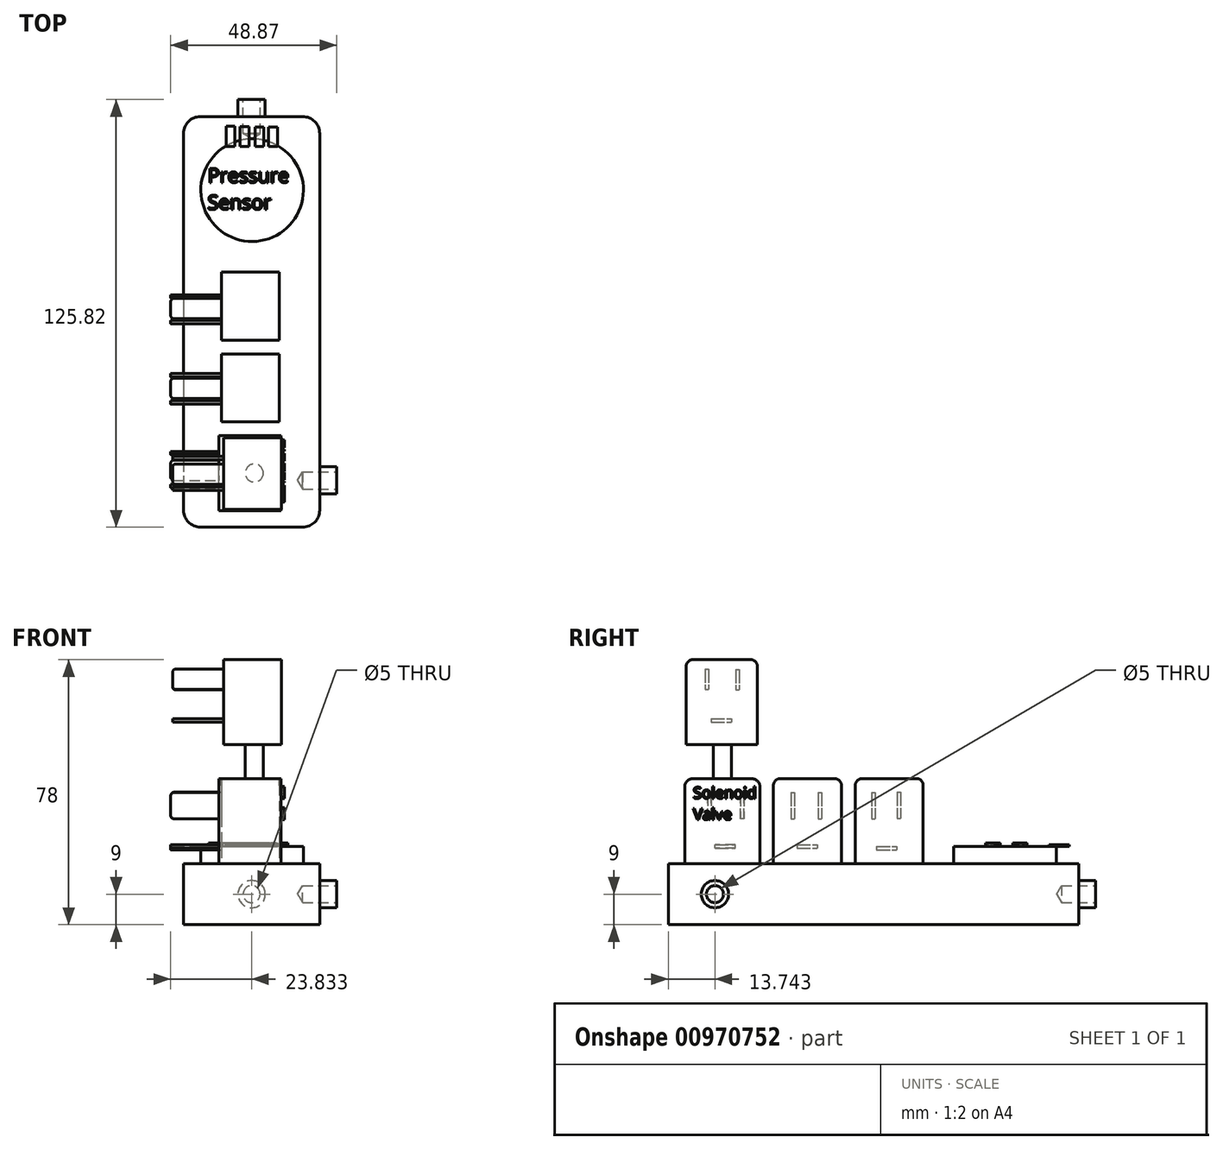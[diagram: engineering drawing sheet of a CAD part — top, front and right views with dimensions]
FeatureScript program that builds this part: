
annotation { "Feature Type Name" : "Feature", "Feature Type Description" : "" }
export const myFeature = defineFeature(function(context is Context, id is Id, definition is map)
    precondition{}
    {
        {
            var Q0;
            Q0=qCreatedBy(makeId("Top.planeOp"),FACE);
            var sketch = newSketch(context, id + "F0", { "sketchPlane" : qUnion([Q0])});
            skLineSegment(sketch, "E0", {"start": v(-31.16, -51.49) * mm, "end": v(8.92, -51.49) * mm});
            skLineSegment(sketch, "E1", {"start": v(8.92, -51.49) * mm, "end": v(8.92, 69.33) * mm});
            skLineSegment(sketch, "E2", {"start": v(8.92, 69.33) * mm, "end": v(-31.16, 69.33) * mm});
            skLineSegment(sketch, "E3", {"start": v(-31.16, 69.33) * mm, "end": v(-31.16, -51.49) * mm});
            skSolve(sketch);
        }
        {
            var Q0;
            Q0=makeQuery(id+"F0.imprint","IMPRINT",FACE,{"disambiguationData":[TD([[makeQuery(id+"F0.imprint","IMPRINT",EDGE,{"derivedFrom":sQuery(id+"F0.wireOp",EDGE,"E0")}),1.0]])]});
            extrude(context, id + "F1", {"entities" : qUnion([Q0]), "depth" : 18 * mm, "offsetDistance" : 25 * mm});
        }
        {
            var Q0;
            Q0=makeQuery(id+"F1.opExtrude","CAP_FACE",FACE,{"disambiguationData":[OSD([sQuery(id+"F0.wireOp",EDGE,"E0"),sQuery(id+"F0.wireOp",EDGE,"E1"),sQuery(id+"F0.wireOp",EDGE,"E2"),sQuery(id+"F0.wireOp",EDGE,"E3")])],"isStart":false});
            var sketch = newSketch(context, id + "F2", { "sketchPlane" : qUnion([Q0])});
            skCircle(sketch, "E4", {"center": v(-10.96, 47.67) * mm, "radius": 15.1 * mm});
            skSolve(sketch);
        }
        {
            var Q0;
            Q0=makeQuery(id+"F2.imprint","IMPRINT",FACE,{"disambiguationData":[TD([[makeQuery(id+"F2.imprint","IMPRINT",EDGE,{"derivedFrom":sQuery(id+"F2.wireOp",EDGE,"E4")}),1.0]])]});
            extrude(context, id + "F3", {"entities" : qUnion([Q0]), "operationType" : NewBodyOperationType.ADD, "depth" : 5 * mm, "offsetDistance" : 25 * mm});
        }
        {
            var Q0;
            Q0=makeQuery(id+"F3.opExtrude","CAP_FACE",FACE,{"disambiguationData":[OSD([sQuery(id+"F2.wireOp",EDGE,"E4")])],"isStart":false});
            var sketch = newSketch(context, id + "F4", { "sketchPlane" : qUnion([Q0])});
            skLineSegment(sketch, "E5", {"start": v(-14.48, 60.58) * mm, "end": v(-11.85, 60.58) * mm});
            skLineSegment(sketch, "E6", {"start": v(-11.85, 60.58) * mm, "end": v(-11.85, 66.33) * mm});
            skLineSegment(sketch, "E7", {"start": v(-11.85, 66.33) * mm, "end": v(-14.55, 66.33) * mm});
            skLineSegment(sketch, "E8", {"start": v(-14.55, 66.33) * mm, "end": v(-14.48, 60.58) * mm});
            skSolve(sketch);
        }
        {
            var Q0;
            {var subQ0=sQuery(id+"F4.wireOp",EDGE,"E7");Q0=makeQuery(id+"F4.imprint","IMPRINT",FACE,{"disambiguationData":[TD([[makeQuery(id+"F4.imprint","IMPRINT",EDGE,{"derivedFrom":subQ0}),1.0]])]});}
            var Q1;
            {var subQ0=sQuery(id+"F4.wireOp",EDGE,"E5");Q1=makeQuery(id+"F4.imprint","IMPRINT",FACE,{"disambiguationData":[TD([[makeQuery(id+"F4.imprint","IMPRINT",EDGE,{"derivedFrom":subQ0}),1.0]])]});}
            extrude(context, id + "F5", {"entities" : qUnion([Q0, Q1]), "operationType" : NewBodyOperationType.ADD, "depth" : 0.5 * mm, "offsetDistance" : 25 * mm});
        }
        {
            var Q0;
            Q0=makeQuery(id+"F3.opExtrude","CAP_FACE",FACE,{"disambiguationData":[OSD([sQuery(id+"F2.wireOp",EDGE,"E4")])],"isStart":false});
            var sketch = newSketch(context, id + "F6", { "sketchPlane" : qUnion([Q0])});
            skLineSegment(sketch, "E9", {"start": v(-16.09, 60.58) * mm, "end": v(-18.63, 60.58) * mm});
            skLineSegment(sketch, "E10", {"start": v(-18.63, 60.58) * mm, "end": v(-18.63, 66.5) * mm});
            skLineSegment(sketch, "E11", {"start": v(-18.63, 66.5) * mm, "end": v(-16.09, 66.5) * mm});
            skLineSegment(sketch, "E12", {"start": v(-16.09, 66.5) * mm, "end": v(-16.09, 60.58) * mm});
            skSolve(sketch);
        }
        {
            var Q0;
            {var subQ0=sQuery(id+"F6.wireOp",EDGE,"E9");Q0=makeQuery(id+"F6.imprint","IMPRINT",FACE,{"disambiguationData":[TD([[makeQuery(id+"F6.imprint","IMPRINT",EDGE,{"derivedFrom":subQ0}),-1.0]])]});}
            var Q1;
            {var subQ0=sQuery(id+"F6.wireOp",EDGE,"E11");Q1=makeQuery(id+"F6.imprint","IMPRINT",FACE,{"disambiguationData":[TD([[makeQuery(id+"F6.imprint","IMPRINT",EDGE,{"derivedFrom":subQ0}),-1.0]])]});}
            extrude(context, id + "F7", {"entities" : qUnion([Q0, Q1]), "operationType" : NewBodyOperationType.ADD, "depth" : 0.5 * mm, "offsetDistance" : 25 * mm});
        }
        {
            var Q0;
            Q0=makeQuery(id+"F3.opExtrude","CAP_FACE",FACE,{"disambiguationData":[OSD([sQuery(id+"F2.wireOp",EDGE,"E4")])],"isStart":false});
            var sketch = newSketch(context, id + "F8", { "sketchPlane" : qUnion([Q0])});
            skLineSegment(sketch, "E13", {"start": v(-10.12, 60.58) * mm, "end": v(-7.57, 60.58) * mm});
            skLineSegment(sketch, "E14", {"start": v(-7.57, 60.58) * mm, "end": v(-7.57, 66.29) * mm});
            skLineSegment(sketch, "E15", {"start": v(-7.57, 66.29) * mm, "end": v(-10.12, 66.29) * mm});
            skLineSegment(sketch, "E16", {"start": v(-10.12, 66.29) * mm, "end": v(-10.12, 60.58) * mm});
            skSolve(sketch);
        }
        {
            var Q0;
            {var subQ0=sQuery(id+"F8.wireOp",EDGE,"E15");Q0=makeQuery(id+"F8.imprint","IMPRINT",FACE,{"disambiguationData":[TD([[makeQuery(id+"F8.imprint","IMPRINT",EDGE,{"derivedFrom":subQ0}),1.0]])]});}
            var Q1;
            {var subQ0=sQuery(id+"F8.wireOp",EDGE,"E13");Q1=makeQuery(id+"F8.imprint","IMPRINT",FACE,{"disambiguationData":[TD([[makeQuery(id+"F8.imprint","IMPRINT",EDGE,{"derivedFrom":subQ0}),1.0]])]});}
            extrude(context, id + "F9", {"entities" : qUnion([Q0, Q1]), "operationType" : NewBodyOperationType.ADD, "depth" : 0.5 * mm, "offsetDistance" : 25 * mm});
        }
        {
            var Q0;
            Q0=makeQuery(id+"F3.opExtrude","CAP_FACE",FACE,{"disambiguationData":[OSD([sQuery(id+"F2.wireOp",EDGE,"E4")])],"isStart":false});
            var sketch = newSketch(context, id + "F10", { "sketchPlane" : qUnion([Q0])});
            skText(sketch, "E17", { "text": "Pressure\nSensor", "fontName": "OpenSans-Regular.ttf"});
            const initialGuessF10  = {"E17": [-0.02405, 0.04993, 1, 0, 0.0042]};
            skSetInitialGuess(sketch, initialGuessF10);
            skSolve(sketch);
        }
        {
            var Q0;
            Q0=qSketchRegion(id+"F10",true);
            extrude(context, id + "F11", {"entities" : qUnion([Q0]), "operationType" : NewBodyOperationType.ADD, "depth" : 1 * mm, "offsetDistance" : 25 * mm});
        }
        {
            var Q0;
            Q0=makeQuery(id+"F1.opExtrude","SWEPT_FACE",FACE,{"disambiguationData":[OSD([sQuery(id+"F0.wireOp",EDGE,"E2")])]});
            var sketch = newSketch(context, id + "F12", { "sketchPlane" : qUnion([Q0])});
            skCircle(sketch, "E18", {"center": v(11.12, 9) * mm, "radius": 4 * mm});
            skPoint(sketch, "E18.centerSnap0", {"position": v(31.16, 9) * mm});
            skPoint(sketch, "E18.centerSnap1", {"position": v(11.12, 18) * mm});
            skSolve(sketch);
        }
        {
            var Q0;
            Q0=makeQuery(id+"F12.imprint","IMPRINT",FACE,{"disambiguationData":[TD([[makeQuery(id+"F12.imprint","IMPRINT",EDGE,{"derivedFrom":sQuery(id+"F12.wireOp",EDGE,"E18")}),1.0]])]});
            extrude(context, id + "F13", {"entities" : qUnion([Q0]), "operationType" : NewBodyOperationType.ADD, "depth" : 5 * mm, "offsetDistance" : 25 * mm});
        }
        {
            var Q0;
            Q0=makeQuery(id+"F13.opExtrude","CAP_FACE",FACE,{"disambiguationData":[OSD([sQuery(id+"F12.wireOp",EDGE,"E18")])],"isStart":false});
            var sketch = newSketch(context, id + "F14", { "sketchPlane" : qUnion([Q0])});
            skCircle(sketch, "E19", {"center": v(11.12, 9) * mm, "radius": 2.5 * mm});
            skSolve(sketch);
        }
        {
            var Q0;
            Q0=sQuery(id+"F14.wireOp",VERTEX,"E19.center");
            var Q1;
            Q1=makeQuery(id+"F1.opExtrude","SWEPT_BODY",BODY,{"disambiguationData":[OSD([sQuery(id+"F0.wireOp",EDGE,"E0"),sQuery(id+"F0.wireOp",EDGE,"E1"),sQuery(id+"F0.wireOp",EDGE,"E2"),sQuery(id+"F0.wireOp",EDGE,"E3")])]});
            hole(context, id + "F15", {"style" : HoleStyle.SIMPLE, "endStyle" : HoleEndStyle.BLIND, "holeDiameter" : 5 * mm, "majorDiameter" : 5 * mm, "holeDepth" : 10 * mm, "isTappedThrough" : true, "tappedDepth" : 12 * mm, "tapClearance" : 3, "locations" : qUnion([Q0]), "scope" : qUnion([Q1])});
        }
        {
            var Q0;
            {var subQ7=sQuery(id+"F2.wireOp",EDGE,"E4");Q0=makeQuery(id+"F11.boolean.opBoolean","SPLIT",FACE,{"disambiguationData":[TD([makeQuery(id+"F3.opExtrude","SWEPT_FACE",FACE,{"disambiguationData":[OSD([subQ7])]})])],"derivedFrom":makeQuery(id+"F3.opExtrude","CAP_FACE",FACE,{"disambiguationData":[OSD([subQ7])],"isStart":false})});}
            var sketch = newSketch(context, id + "F16", { "sketchPlane" : qUnion([Q0])});
            skLineSegment(sketch, "E20.bottom", {"start": v(-6.1, 60.58) * mm, "end": v(-3.42, 60.58) * mm});
            skLineSegment(sketch, "E20.top", {"start": v(-6.1, 66.26) * mm, "end": v(-3.42, 66.26) * mm});
            skLineSegment(sketch, "E20.left", {"start": v(-6.1, 60.58) * mm, "end": v(-6.1, 66.26) * mm});
            skLineSegment(sketch, "E20.right", {"start": v(-3.42, 60.58) * mm, "end": v(-3.42, 66.26) * mm});
            skSolve(sketch);
        }
        {
            var Q0;
            {var subQ0=sQuery(id+"F16.wireOp",EDGE,"E20.bottom");Q0=makeQuery(id+"F16.imprint","IMPRINT",FACE,{"disambiguationData":[TD([[makeQuery(id+"F16.imprint","IMPRINT",EDGE,{"derivedFrom":subQ0}),1.0]])]});}
            var Q1;
            {var subQ0=sQuery(id+"F16.wireOp",EDGE,"E20.top");Q1=makeQuery(id+"F16.imprint","IMPRINT",FACE,{"disambiguationData":[TD([[makeQuery(id+"F16.imprint","IMPRINT",EDGE,{"derivedFrom":subQ0}),-1.0]])]});}
            extrude(context, id + "F17", {"entities" : qUnion([Q0, Q1]), "operationType" : NewBodyOperationType.ADD, "depth" : 0.5 * mm, "offsetDistance" : 25 * mm});
        }
        {
            var Q0;
            Q0=makeQuery(id+"F1.opExtrude","SWEPT_FACE",FACE,{"disambiguationData":[OSD([sQuery(id+"F0.wireOp",EDGE,"E1")])]});
            var sketch = newSketch(context, id + "F18", { "sketchPlane" : qUnion([Q0])});
            skCircle(sketch, "E21", {"center": v(-37.75, 9) * mm, "radius": 4 * mm});
            skPoint(sketch, "E21.centerSnap0", {"position": v(-51.49, 9) * mm});
            skSolve(sketch);
        }
        {
            var Q0;
            Q0=makeQuery(id+"F18.imprint","IMPRINT",FACE,{"disambiguationData":[TD([[makeQuery(id+"F18.imprint","IMPRINT",EDGE,{"derivedFrom":sQuery(id+"F18.wireOp",EDGE,"E21")}),1.0]])]});
            extrude(context, id + "F19", {"entities" : qUnion([Q0]), "operationType" : NewBodyOperationType.ADD, "depth" : 5 * mm, "offsetDistance" : 25 * mm});
        }
        {
            var Q0;
            Q0=makeQuery(id+"F19.opExtrude","CAP_FACE",FACE,{"disambiguationData":[OSD([sQuery(id+"F18.wireOp",EDGE,"E21")])],"isStart":false});
            var sketch = newSketch(context, id + "F20", { "sketchPlane" : qUnion([Q0])});
            skCircle(sketch, "E22", {"center": v(-37.75, 9) * mm, "radius": 2.01 * mm});
            skSolve(sketch);
        }
        {
            var Q0;
            Q0=sQuery(id+"F20.wireOp",VERTEX,"E22.center");
            var Q1;
            Q1=makeQuery(id+"F1.opExtrude","SWEPT_BODY",BODY,{"disambiguationData":[OSD([sQuery(id+"F0.wireOp",EDGE,"E0"),sQuery(id+"F0.wireOp",EDGE,"E1"),sQuery(id+"F0.wireOp",EDGE,"E2"),sQuery(id+"F0.wireOp",EDGE,"E3")])]});
            hole(context, id + "F21", {"style" : HoleStyle.SIMPLE, "endStyle" : HoleEndStyle.BLIND, "holeDiameter" : 5 * mm, "majorDiameter" : 5 * mm, "holeDepth" : 10 * mm, "isTappedThrough" : true, "tappedDepth" : 12 * mm, "tapClearance" : 3, "locations" : qUnion([Q0]), "scope" : qUnion([Q1])});
        }
        {
            var Q0;
            Q0=makeQuery(id+"F1.opExtrude","SWEPT_EDGE",EDGE,{"disambiguationData":[OSD([sQuery(id+"F0.wireOp",EDGE,"E1"),sQuery(id+"F0.wireOp",EDGE,"E2")])]});
            fillet(context, id + "F22", {"entities" : qUnion([Q0]), "radius" : 5 * mm, "tangentPropagation" : true, "allowEdgeOverflow" : false});
        }
        {
            var Q0;
            Q0=makeQuery(id+"F1.opExtrude","SWEPT_EDGE",EDGE,{"disambiguationData":[OSD([sQuery(id+"F0.wireOp",EDGE,"E2"),sQuery(id+"F0.wireOp",EDGE,"E3")])]});
            fillet(context, id + "F23", {"entities" : qUnion([Q0]), "radius" : 5 * mm, "tangentPropagation" : true, "allowEdgeOverflow" : false});
        }
        {
            var Q0;
            Q0=makeQuery(id+"F1.opExtrude","SWEPT_EDGE",EDGE,{"disambiguationData":[OSD([sQuery(id+"F0.wireOp",EDGE,"E0"),sQuery(id+"F0.wireOp",EDGE,"E3")])]});
            fillet(context, id + "F24", {"entities" : qUnion([Q0]), "radius" : 5 * mm, "tangentPropagation" : true, "allowEdgeOverflow" : false});
        }
        {
            var Q0;
            Q0=makeQuery(id+"F1.opExtrude","SWEPT_EDGE",EDGE,{"disambiguationData":[OSD([sQuery(id+"F0.wireOp",EDGE,"E0"),sQuery(id+"F0.wireOp",EDGE,"E1")])]});
            fillet(context, id + "F25", {"entities" : qUnion([Q0]), "radius" : 5 * mm, "tangentPropagation" : true, "allowEdgeOverflow" : false});
        }
        {
            var Q0;
            Q0=makeQuery(id+"F1.opExtrude","CAP_FACE",FACE,{"disambiguationData":[OSD([sQuery(id+"F0.wireOp",EDGE,"E0"),sQuery(id+"F0.wireOp",EDGE,"E1"),sQuery(id+"F0.wireOp",EDGE,"E2"),sQuery(id+"F0.wireOp",EDGE,"E3")])],"isStart":false});
            var sketch = newSketch(context, id + "F26", { "sketchPlane" : qUnion([Q0])});
            skLineSegment(sketch, "E23.bottom", {"start": v(-20.72, -46.66) * mm, "end": v(-2.41, -46.66) * mm});
            skLineSegment(sketch, "E23.top", {"start": v(-20.72, -24.5) * mm, "end": v(-2.41, -24.5) * mm});
            skLineSegment(sketch, "E23.left", {"start": v(-20.72, -46.66) * mm, "end": v(-20.72, -24.5) * mm});
            skLineSegment(sketch, "E23.right", {"start": v(-2.41, -46.66) * mm, "end": v(-2.41, -24.5) * mm});
            skSolve(sketch);
        }
        {
            var Q0;
            Q0=makeQuery(id+"F26.imprint","IMPRINT",FACE,{"disambiguationData":[TD([[makeQuery(id+"F26.imprint","IMPRINT",EDGE,{"derivedFrom":sQuery(id+"F26.wireOp",EDGE,"E23.bottom")}),1.0]])]});
            extrude(context, id + "F27", {"entities" : qUnion([Q0]), "operationType" : NewBodyOperationType.ADD, "depth" : 25 * mm, "offsetDistance" : 25 * mm});
        }
        {
            var Q0;
            Q0=makeQuery(id+"F27.opExtrude","CAP_EDGE",EDGE,{"disambiguationData":[OSD([sQuery(id+"F26.wireOp",EDGE,"E23.bottom")])],"isStart":false});
            var Q1;
            Q1=makeQuery(id+"F27.opExtrude","CAP_EDGE",EDGE,{"disambiguationData":[OSD([sQuery(id+"F26.wireOp",EDGE,"E23.top")])],"isStart":false});
            fillet(context, id + "F28", {"entities" : qUnion([Q0, Q1]), "radius" : 2.5 * mm, "tangentPropagation" : true, "allowEdgeOverflow" : false});
        }
        {
            var Q0;
            Q0=makeQuery(id+"F27.opExtrude","SWEPT_FACE",FACE,{"disambiguationData":[OSD([sQuery(id+"F26.wireOp",EDGE,"E23.right")])]});
            var sketch = newSketch(context, id + "F29", { "sketchPlane" : qUnion([Q0])});
            skText(sketch, "E24", { "text": "Solenoid\nValve", "fontName": "OpenSans-Regular.ttf"});
            const initialGuessF29  = {"E24": [-0.04416, 0.03718, 1, 0, 0.00332]};
            skSetInitialGuess(sketch, initialGuessF29);
            skSolve(sketch);
        }
        {
            var Q0;
            Q0=qSketchRegion(id+"F29",true);
            extrude(context, id + "F30", {"entities" : qUnion([Q0]), "operationType" : NewBodyOperationType.ADD, "depth" : 1 * mm, "offsetDistance" : 25 * mm});
        }
        {
            var Q0;
            Q0=makeQuery(id+"F1.opExtrude","CAP_FACE",FACE,{"disambiguationData":[OSD([sQuery(id+"F0.wireOp",EDGE,"E0"),sQuery(id+"F0.wireOp",EDGE,"E1"),sQuery(id+"F0.wireOp",EDGE,"E2"),sQuery(id+"F0.wireOp",EDGE,"E3")])],"isStart":false});
            var sketch = newSketch(context, id + "F31", { "sketchPlane" : qUnion([Q0])});
            skLineSegment(sketch, "E25.bottom", {"start": v(-3, -0.51) * mm, "end": v(-20, -0.51) * mm});
            skLineSegment(sketch, "E25.top", {"start": v(-3, -20.51) * mm, "end": v(-20, -20.51) * mm});
            skLineSegment(sketch, "E25.left", {"start": v(-3, -0.51) * mm, "end": v(-3, -20.51) * mm});
            skLineSegment(sketch, "E25.right", {"start": v(-20, -0.51) * mm, "end": v(-20, -20.51) * mm});
            skLineSegment(sketch, "E26.bottom", {"start": v(-2.95, 23.55) * mm, "end": v(-19.95, 23.55) * mm});
            skLineSegment(sketch, "E26.top", {"start": v(-2.95, 3.55) * mm, "end": v(-19.95, 3.55) * mm});
            skLineSegment(sketch, "E26.left", {"start": v(-2.95, 23.55) * mm, "end": v(-2.95, 3.55) * mm});
            skLineSegment(sketch, "E26.right", {"start": v(-19.95, 23.55) * mm, "end": v(-19.95, 3.55) * mm});
            skSolve(sketch);
        }
        {
            var Q0;
            Q0 = qSketchRegion(id + "F31", true);
            extrude(context, id + "F32", {"entities" : qUnion([Q0]), "operationType" : NewBodyOperationType.ADD, "depth" : 25 * mm, "offsetDistance" : 25 * mm});
        }
        {
            var Q0;
            Q0=makeQuery(id+"F32.opExtrude","CAP_EDGE",EDGE,{"disambiguationData":[OSD([sQuery(id+"F31.wireOp",EDGE,"E25.bottom")])],"isStart":false});
            var Q1;
            Q1=makeQuery(id+"F32.opExtrude","CAP_EDGE",EDGE,{"disambiguationData":[OSD([sQuery(id+"F31.wireOp",EDGE,"E25.top")])],"isStart":false});
            var Q2;
            Q2=makeQuery(id+"F32.opExtrude","CAP_EDGE",EDGE,{"disambiguationData":[OSD([sQuery(id+"F31.wireOp",EDGE,"E26.top")])],"isStart":false});
            var Q3;
            Q3=makeQuery(id+"F32.opExtrude","CAP_EDGE",EDGE,{"disambiguationData":[OSD([sQuery(id+"F31.wireOp",EDGE,"E26.bottom")])],"isStart":false});
            fillet(context, id + "F33", {"entities" : qUnion([Q0, Q1, Q2, Q3]), "radius" : 2 * mm, "tangentPropagation" : true, "allowEdgeOverflow" : false});
        }
        {
            var Q0;
            Q0=makeQuery(id+"F32.opExtrude","SWEPT_FACE",FACE,{"disambiguationData":[OSD([sQuery(id+"F31.wireOp",EDGE,"E26.right")])]});
            cPlane(context, id + "F34", {"entities" : qUnion([Q0]), "cplaneType" : CPlaneType.OFFSET, "offset" : 0 * mm, "width" : 150 * mm, "height" : 150 * mm});
        }
        {
            var Q0;
            Q0=qCreatedBy(id+"F34.planeOp",FACE);
            var sketch = newSketch(context, id + "F35", { "sketchPlane" : qUnion([Q0])});
            skLineSegment(sketch, "E27.bottom", {"start": v(-8.35, 38.88) * mm, "end": v(-9.35, 38.88) * mm});
            skLineSegment(sketch, "E27.top", {"start": v(-8.35, 31.16) * mm, "end": v(-9.35, 31.16) * mm});
            skLineSegment(sketch, "E27.left", {"start": v(-8.35, 38.88) * mm, "end": v(-8.35, 31.16) * mm});
            skLineSegment(sketch, "E27.right", {"start": v(-9.35, 38.88) * mm, "end": v(-9.35, 31.16) * mm});
            skLineSegment(sketch, "E28.bottom", {"start": v(-15.9, 38.98) * mm, "end": v(-16.9, 38.98) * mm});
            skLineSegment(sketch, "E28.top", {"start": v(-15.9, 31.26) * mm, "end": v(-16.9, 31.26) * mm});
            skLineSegment(sketch, "E28.left", {"start": v(-15.9, 38.98) * mm, "end": v(-15.9, 31.26) * mm});
            skLineSegment(sketch, "E28.right", {"start": v(-16.9, 38.98) * mm, "end": v(-16.9, 31.26) * mm});
            skLineSegment(sketch, "E29.bottom", {"start": v(15.3, 38.88) * mm, "end": v(14.3, 38.88) * mm});
            skLineSegment(sketch, "E29.top", {"start": v(15.3, 31.16) * mm, "end": v(14.3, 31.16) * mm});
            skLineSegment(sketch, "E29.left", {"start": v(15.3, 38.88) * mm, "end": v(15.3, 31.16) * mm});
            skLineSegment(sketch, "E29.right", {"start": v(14.3, 38.88) * mm, "end": v(14.3, 31.16) * mm});
            skLineSegment(sketch, "E30.bottom", {"start": v(7.3, 38.88) * mm, "end": v(6.3, 38.88) * mm});
            skLineSegment(sketch, "E30.top", {"start": v(7.3, 31.16) * mm, "end": v(6.3, 31.16) * mm});
            skLineSegment(sketch, "E30.left", {"start": v(7.3, 38.88) * mm, "end": v(7.3, 31.16) * mm});
            skLineSegment(sketch, "E30.right", {"start": v(6.3, 38.88) * mm, "end": v(6.3, 31.16) * mm});
            skLineSegment(sketch, "E31.bottom", {"start": v(30.2, 38.87) * mm, "end": v(29.2, 38.87) * mm});
            skLineSegment(sketch, "E31.top", {"start": v(30.2, 31.15) * mm, "end": v(29.2, 31.15) * mm});
            skLineSegment(sketch, "E31.left", {"start": v(30.2, 38.87) * mm, "end": v(30.2, 31.15) * mm});
            skLineSegment(sketch, "E31.right", {"start": v(29.2, 38.87) * mm, "end": v(29.2, 31.15) * mm});
            skLineSegment(sketch, "E32.bottom", {"start": v(39.9, 38.91) * mm, "end": v(38.9, 38.91) * mm});
            skLineSegment(sketch, "E32.top", {"start": v(39.9, 31.19) * mm, "end": v(38.9, 31.19) * mm});
            skLineSegment(sketch, "E32.left", {"start": v(39.9, 38.91) * mm, "end": v(39.9, 31.19) * mm});
            skLineSegment(sketch, "E32.right", {"start": v(38.9, 38.91) * mm, "end": v(38.9, 31.19) * mm});
            skLineSegment(sketch, "E33.bottom", {"start": v(37.73, 23.51) * mm, "end": v(31.73, 23.51) * mm});
            skLineSegment(sketch, "E33.top", {"start": v(37.73, 22.51) * mm, "end": v(31.73, 22.51) * mm});
            skLineSegment(sketch, "E33.left", {"start": v(37.73, 23.51) * mm, "end": v(37.73, 22.51) * mm});
            skLineSegment(sketch, "E33.right", {"start": v(31.73, 23.51) * mm, "end": v(31.73, 22.51) * mm});
            skLineSegment(sketch, "E34.bottom", {"start": v(13.65, 23.52) * mm, "end": v(7.65, 23.52) * mm});
            skLineSegment(sketch, "E34.top", {"start": v(13.65, 22.52) * mm, "end": v(7.65, 22.52) * mm});
            skLineSegment(sketch, "E34.left", {"start": v(13.65, 23.52) * mm, "end": v(13.65, 22.52) * mm});
            skLineSegment(sketch, "E34.right", {"start": v(7.65, 23.52) * mm, "end": v(7.65, 22.52) * mm});
            skLineSegment(sketch, "E35.bottom", {"start": v(-9.82, 23.03) * mm, "end": v(-15.82, 23.03) * mm});
            skLineSegment(sketch, "E35.top", {"start": v(-9.82, 22.03) * mm, "end": v(-15.82, 22.03) * mm});
            skLineSegment(sketch, "E35.left", {"start": v(-9.82, 23.03) * mm, "end": v(-9.82, 22.03) * mm});
            skLineSegment(sketch, "E35.right", {"start": v(-15.82, 23.03) * mm, "end": v(-15.82, 22.03) * mm});
            skSolve(sketch);
        }
        {
            var Q0;
            Q0 = qSketchRegion(id + "F35", true);
            extrude(context, id + "F36", {"entities" : qUnion([Q0]), "operationType" : NewBodyOperationType.ADD, "depth" : 15 * mm, "offsetDistance" : 25 * mm});
        }
        {
            var Q0;
            Q0=makeQuery(id+"F27.opExtrude","CAP_FACE",FACE,{"disambiguationData":[OSD([sQuery(id+"F26.wireOp",EDGE,"E23.bottom"),sQuery(id+"F26.wireOp",EDGE,"E23.top"),sQuery(id+"F26.wireOp",EDGE,"E23.left"),sQuery(id+"F26.wireOp",EDGE,"E23.right")])],"isStart":false});
            var sketch = newSketch(context, id + "F37", { "sketchPlane" : qUnion([Q0])});
            skCircle(sketch, "E36", {"center": v(-10.33, -35.58) * mm, "radius": 2.67 * mm});
            skPoint(sketch, "E36.centerSnap0", {"position": v(-2.41, -35.58) * mm});
            skSolve(sketch);
        }
        {
            var Q0;
            Q0 = qSketchRegion(id + "F37", true);
            extrude(context, id + "F38", {"entities" : qUnion([Q0]), "operationType" : NewBodyOperationType.ADD, "depth" : 10 * mm, "offsetDistance" : 25 * mm});
        }
        {
            var Q0;
            Q0=makeQuery(id+"F38.opExtrude","CAP_FACE",FACE,{"disambiguationData":[OSD([sQuery(id+"F37.wireOp",EDGE,"E36")])],"isStart":false});
            var sketch = newSketch(context, id + "F39", { "sketchPlane" : qUnion([Q0])});
            skLineSegment(sketch, "E37.bottom", {"start": v(-2.4, -46.23) * mm, "end": v(-19.4, -46.23) * mm});
            skLineSegment(sketch, "E37.top", {"start": v(-2.4, -25.23) * mm, "end": v(-19.4, -25.23) * mm});
            skLineSegment(sketch, "E37.left", {"start": v(-2.4, -46.23) * mm, "end": v(-2.4, -25.23) * mm});
            skLineSegment(sketch, "E37.right", {"start": v(-19.4, -46.23) * mm, "end": v(-19.4, -25.23) * mm});
            skSolve(sketch);
        }
        {
            var Q0;
            Q0 = qSketchRegion(id + "F39", true);
            extrude(context, id + "F40", {"entities" : qUnion([Q0]), "operationType" : NewBodyOperationType.ADD, "depth" : 25 * mm, "offsetDistance" : 25 * mm});
        }
        {
            var Q0;
            Q0=makeQuery(id+"F40.opExtrude","CAP_EDGE",EDGE,{"disambiguationData":[OSD([sQuery(id+"F39.wireOp",EDGE,"E37.top")])],"isStart":false});
            var Q1;
            Q1=makeQuery(id+"F40.opExtrude","CAP_EDGE",EDGE,{"disambiguationData":[OSD([sQuery(id+"F39.wireOp",EDGE,"E37.bottom")])],"isStart":false});
            fillet(context, id + "F41", {"entities" : qUnion([Q0, Q1]), "radius" : 2 * mm, "tangentPropagation" : true, "allowEdgeOverflow" : false});
        }
        {
            var Q0;
            Q0=makeQuery(id+"F40.opExtrude","SWEPT_FACE",FACE,{"disambiguationData":[OSD([sQuery(id+"F39.wireOp",EDGE,"E37.right")])]});
            var sketch = newSketch(context, id + "F42", { "sketchPlane" : qUnion([Q0])});
            skLineSegment(sketch, "E38.bottom", {"start": v(40.66, 75.23) * mm, "end": v(39.66, 75.23) * mm});
            skLineSegment(sketch, "E38.top", {"start": v(40.66, 69.23) * mm, "end": v(39.66, 69.23) * mm});
            skLineSegment(sketch, "E38.left", {"start": v(40.66, 75.23) * mm, "end": v(40.66, 69.23) * mm});
            skLineSegment(sketch, "E38.right", {"start": v(39.66, 75.23) * mm, "end": v(39.66, 69.23) * mm});
            skLineSegment(sketch, "E39.bottom", {"start": v(31.66, 75.08) * mm, "end": v(30.66, 75.08) * mm});
            skLineSegment(sketch, "E39.top", {"start": v(31.66, 69.08) * mm, "end": v(30.66, 69.08) * mm});
            skLineSegment(sketch, "E39.left", {"start": v(31.66, 75.08) * mm, "end": v(31.66, 69.08) * mm});
            skLineSegment(sketch, "E39.right", {"start": v(30.66, 75.08) * mm, "end": v(30.66, 69.08) * mm});
            skLineSegment(sketch, "E40.bottom", {"start": v(38.9, 60.57) * mm, "end": v(32.9, 60.57) * mm});
            skLineSegment(sketch, "E40.top", {"start": v(38.9, 59.57) * mm, "end": v(32.9, 59.57) * mm});
            skLineSegment(sketch, "E40.left", {"start": v(38.9, 60.57) * mm, "end": v(38.9, 59.57) * mm});
            skLineSegment(sketch, "E40.right", {"start": v(32.9, 60.57) * mm, "end": v(32.9, 59.57) * mm});
            skSolve(sketch);
        }
        {
            var Q0;
            Q0 = qSketchRegion(id + "F42", true);
            extrude(context, id + "F43", {"entities" : qUnion([Q0]), "operationType" : NewBodyOperationType.ADD, "depth" : 15 * mm, "offsetDistance" : 25 * mm});
        }
        {
            var Q0;
            Q0=makeQuery(id+"F36.opExtrude","CAP_EDGE",EDGE,{"disambiguationData":[OSD([sQuery(id+"F35.wireOp",EDGE,"E35.left")])],"isStart":false});
            var Q1;
            Q1=makeQuery(id+"F36.opExtrude","CAP_EDGE",EDGE,{"disambiguationData":[OSD([sQuery(id+"F35.wireOp",EDGE,"E35.right")])],"isStart":false});
            var Q2;
            Q2=makeQuery(id+"F36.opExtrude","CAP_EDGE",EDGE,{"disambiguationData":[OSD([sQuery(id+"F35.wireOp",EDGE,"E28.top")])],"isStart":false});
            var Q3;
            Q3=makeQuery(id+"F36.opExtrude","CAP_EDGE",EDGE,{"disambiguationData":[OSD([sQuery(id+"F35.wireOp",EDGE,"E27.top")])],"isStart":false});
            var Q4;
            Q4=makeQuery(id+"F36.opExtrude","CAP_EDGE",EDGE,{"disambiguationData":[OSD([sQuery(id+"F35.wireOp",EDGE,"E27.bottom")])],"isStart":false});
            var Q5;
            Q5=makeQuery(id+"F36.opExtrude","CAP_EDGE",EDGE,{"disambiguationData":[OSD([sQuery(id+"F35.wireOp",EDGE,"E28.bottom")])],"isStart":false});
            var Q6;
            Q6=makeQuery(id+"F36.opExtrude","CAP_EDGE",EDGE,{"disambiguationData":[OSD([sQuery(id+"F35.wireOp",EDGE,"E30.bottom")])],"isStart":false});
            var Q7;
            Q7=makeQuery(id+"F36.opExtrude","CAP_EDGE",EDGE,{"disambiguationData":[OSD([sQuery(id+"F35.wireOp",EDGE,"E30.top")])],"isStart":false});
            var Q8;
            Q8=makeQuery(id+"F36.opExtrude","CAP_EDGE",EDGE,{"disambiguationData":[OSD([sQuery(id+"F35.wireOp",EDGE,"E29.top")])],"isStart":false});
            var Q9;
            Q9=makeQuery(id+"F36.opExtrude","CAP_EDGE",EDGE,{"disambiguationData":[OSD([sQuery(id+"F35.wireOp",EDGE,"E29.bottom")])],"isStart":false});
            var Q10;
            Q10=makeQuery(id+"F36.opExtrude","CAP_EDGE",EDGE,{"disambiguationData":[OSD([sQuery(id+"F35.wireOp",EDGE,"E34.left")])],"isStart":false});
            var Q11;
            Q11=makeQuery(id+"F36.opExtrude","CAP_EDGE",EDGE,{"disambiguationData":[OSD([sQuery(id+"F35.wireOp",EDGE,"E34.right")])],"isStart":false});
            var Q12;
            Q12=makeQuery(id+"F36.opExtrude","CAP_EDGE",EDGE,{"disambiguationData":[OSD([sQuery(id+"F35.wireOp",EDGE,"E32.top")])],"isStart":false});
            var Q13;
            Q13=makeQuery(id+"F36.opExtrude","CAP_EDGE",EDGE,{"disambiguationData":[OSD([sQuery(id+"F35.wireOp",EDGE,"E31.top")])],"isStart":false});
            var Q14;
            Q14=makeQuery(id+"F36.opExtrude","CAP_EDGE",EDGE,{"disambiguationData":[OSD([sQuery(id+"F35.wireOp",EDGE,"E31.bottom")])],"isStart":false});
            var Q15;
            Q15=makeQuery(id+"F36.opExtrude","CAP_EDGE",EDGE,{"disambiguationData":[OSD([sQuery(id+"F35.wireOp",EDGE,"E32.bottom")])],"isStart":false});
            var Q16;
            Q16=makeQuery(id+"F36.opExtrude","CAP_EDGE",EDGE,{"disambiguationData":[OSD([sQuery(id+"F35.wireOp",EDGE,"E33.left")])],"isStart":false});
            var Q17;
            Q17=makeQuery(id+"F36.opExtrude","CAP_EDGE",EDGE,{"disambiguationData":[OSD([sQuery(id+"F35.wireOp",EDGE,"E33.right")])],"isStart":false});
            var Q18;
            Q18=makeQuery(id+"F43.opExtrude","CAP_EDGE",EDGE,{"disambiguationData":[OSD([sQuery(id+"F42.wireOp",EDGE,"E40.left")])],"isStart":false});
            var Q19;
            Q19=makeQuery(id+"F43.opExtrude","CAP_EDGE",EDGE,{"disambiguationData":[OSD([sQuery(id+"F42.wireOp",EDGE,"E40.right")])],"isStart":false});
            var Q20;
            Q20=makeQuery(id+"F43.opExtrude","CAP_EDGE",EDGE,{"disambiguationData":[OSD([sQuery(id+"F42.wireOp",EDGE,"E39.bottom")])],"isStart":false});
            var Q21;
            Q21=makeQuery(id+"F43.opExtrude","CAP_EDGE",EDGE,{"disambiguationData":[OSD([sQuery(id+"F42.wireOp",EDGE,"E39.top")])],"isStart":false});
            var Q22;
            Q22=makeQuery(id+"F43.opExtrude","CAP_EDGE",EDGE,{"disambiguationData":[OSD([sQuery(id+"F42.wireOp",EDGE,"E38.top")])],"isStart":false});
            var Q23;
            Q23=makeQuery(id+"F43.opExtrude","CAP_EDGE",EDGE,{"disambiguationData":[OSD([sQuery(id+"F42.wireOp",EDGE,"E38.bottom")])],"isStart":false});
            fillet(context, id + "F44", {"entities" : qUnion([Q0, Q1, Q2, Q3, Q4, Q5, Q6, Q7, Q8, Q9, Q10, Q11, Q12, Q13, Q14, Q15, Q16, Q17, Q18, Q19, Q20, Q21, Q22, Q23]), "radius" : 1 * mm, "tangentPropagation" : true, "allowEdgeOverflow" : false});
        }
    });
